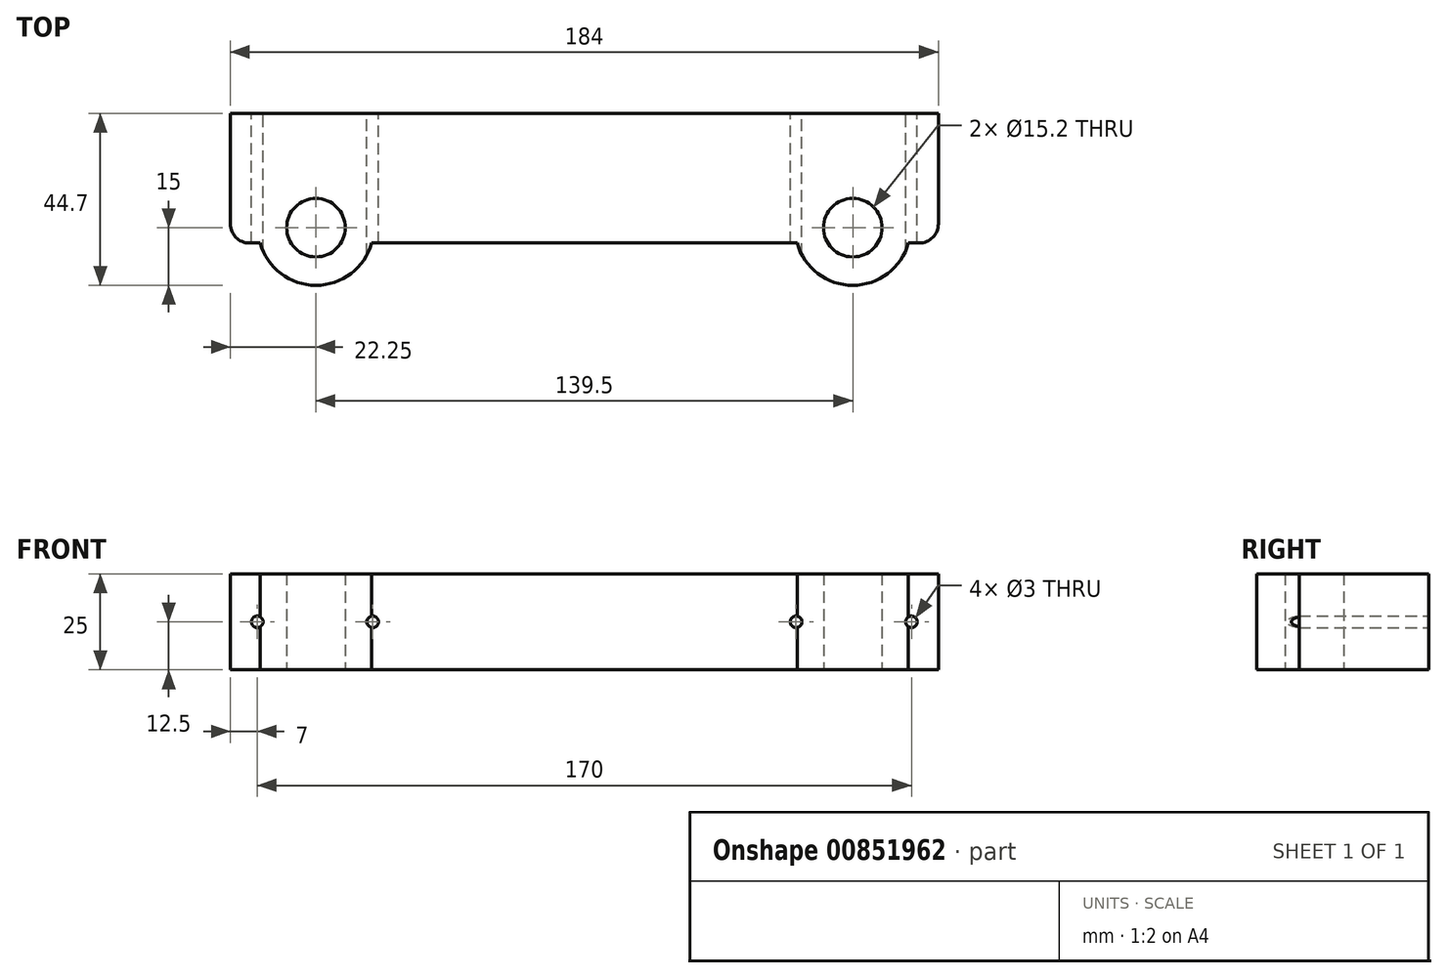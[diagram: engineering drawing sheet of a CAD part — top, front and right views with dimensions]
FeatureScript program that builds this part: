
annotation { "Feature Type Name" : "Feature", "Feature Type Description" : "" }
export const myFeature = defineFeature(function(context is Context, id is Id, definition is map)
    precondition{}
    {
        {
            var Q0;
            Q0=qCreatedBy(makeId("Top.planeOp"),FACE);
            var sketch = newSketch(context, id + "F0", { "sketchPlane" : qUnion([Q0])});
            skLineSegment(sketch, "E0", {"start": v(-69.75, 0) * mm, "end": v(69.75, 0) * mm, "construction": true});
            skCircle(sketch, "E1", {"center": v(-69.75, 0) * mm, "radius": 4 * mm, "construction": true});
            skCircle(sketch, "E2", {"center": v(69.75, 0) * mm, "radius": 4 * mm, "construction": true});
            skCircle(sketch, "E3", {"center": v(-69.75, 0) * mm, "radius": 7.6 * mm});
            skCircle(sketch, "E4", {"center": v(69.75, 0) * mm, "radius": 7.6 * mm});
            skLineSegment(sketch, "E5", {"start": v(0, -4) * mm, "end": v(0, 29.7) * mm, "construction": true});
            skLineSegment(sketch, "E6", {"start": v(-55.3, -4) * mm, "end": v(55.3, -4) * mm});
            skPoint(sketch, "E7", {"position": v(0, 12.5) * mm});
            skLineSegment(sketch, "E8", {"start": v(-55, 29.7) * mm, "end": v(-55, 17.77) * mm, "construction": true});
            skLineSegment(sketch, "E9", {"start": v(55, 29.7) * mm, "end": v(55, 17.82) * mm, "construction": true});
            skLineSegment(sketch, "E10", {"start": v(-92, 29.7) * mm, "end": v(92, 29.7) * mm});
            skLineSegment(sketch, "E11", {"start": v(-85, 29.7) * mm, "end": v(-85, 17.77) * mm, "construction": true});
            skLineSegment(sketch, "E12", {"start": v(-92, 29.7) * mm, "end": v(-92, -4) * mm});
            skArc(sketch, "E13", {"start": v(-84.2, -4) * mm, "mid": v(-69.75, -15) * mm, "end": v(-55.3, -4) * mm});
            skLineSegment(sketch, "E14", {"start": v(-92, -4) * mm, "end": v(-84.2, -4) * mm});
            skArc(sketch, "E15", {"start": v(55.3, -4) * mm, "mid": v(69.75, -15) * mm, "end": v(84.2, -4) * mm});
            skLineSegment(sketch, "E16", {"start": v(92, 29.7) * mm, "end": v(92, -4) * mm});
            skLineSegment(sketch, "E17", {"start": v(92, -4) * mm, "end": v(84.2, -4) * mm});
            skLineSegment(sketch, "E18", {"start": v(85, 29.7) * mm, "end": v(85, 17.82) * mm, "construction": true});
            skSolve(sketch);
        }
        {
            var Q0;
            Q0=makeQuery(id+"F0.imprint","IMPRINT",FACE,{"disambiguationData":[TD([[makeQuery(id+"F0.imprint","IMPRINT",EDGE,{"derivedFrom":sQuery(id+"F0.wireOp",EDGE,"E3")}),-1.0]])]});
            extrude(context, id + "F1", {"entities" : qUnion([Q0]), "depth" : 25 * mm, "offsetDistance" : 25 * mm});
        }
        {
            var Q0;
            Q0=makeQuery(id+"F1.opExtrude","SWEPT_FACE",FACE,{"disambiguationData":[OSD([sQuery(id+"F0.wireOp",EDGE,"E10")])]});
            var sketch = newSketch(context, id + "F2", { "sketchPlane" : qUnion([Q0])});
            skPoint(sketch, "E19.0", {"position": v(55, 0) * mm});
            skPoint(sketch, "E20.0", {"position": v(-55, 0) * mm});
            skLineSegment(sketch, "E21", {"start": v(55, 0) * mm, "end": v(55, 25) * mm, "construction": true});
            skLineSegment(sketch, "E22", {"start": v(-55, 0) * mm, "end": v(-55, 25) * mm, "construction": true});
            skCircle(sketch, "E23", {"center": v(55, 12.5) * mm, "radius": 1.5 * mm});
            skCircle(sketch, "E24", {"center": v(-55, 12.5) * mm, "radius": 1.5 * mm});
            skPoint(sketch, "E25.0", {"position": v(85, 0) * mm});
            skPoint(sketch, "E26.0", {"position": v(-85, 0) * mm});
            skLineSegment(sketch, "E27", {"start": v(85, 0) * mm, "end": v(85, 25) * mm, "construction": true});
            skCircle(sketch, "E28", {"center": v(85, 12.5) * mm, "radius": 1.5 * mm});
            skLineSegment(sketch, "E29", {"start": v(-85, 0) * mm, "end": v(-85, 25) * mm, "construction": true});
            skCircle(sketch, "E30", {"center": v(-85, 12.5) * mm, "radius": 1.5 * mm});
            skSolve(sketch);
        }
        {
            var Q0;
            Q0 = qSketchRegion(id + "F2", true);
            extrude(context, id + "F3", {"entities" : qUnion([Q0]), "operationType" : NewBodyOperationType.REMOVE, "endBound" : BoundingType.THROUGH_ALL, "oppositeDirection" : true, "depth" : 25 * mm, "offsetDistance" : 25 * mm});
        }
        {
            var Q0;
            Q0=makeQuery(id+"F1.opExtrude","SWEPT_EDGE",EDGE,{"disambiguationData":[OSD([sQuery(id+"F0.wireOp",EDGE,"E12"),sQuery(id+"F0.wireOp",EDGE,"E14")])]});
            var Q1;
            Q1=makeQuery(id+"F1.opExtrude","SWEPT_EDGE",EDGE,{"disambiguationData":[OSD([sQuery(id+"F0.wireOp",EDGE,"E16"),sQuery(id+"F0.wireOp",EDGE,"E17")])]});
            fillet(context, id + "F4", {"entities" : qUnion([Q0, Q1]), "radius" : 5 * mm, "tangentPropagation" : true, "allowEdgeOverflow" : false});
        }
    });
